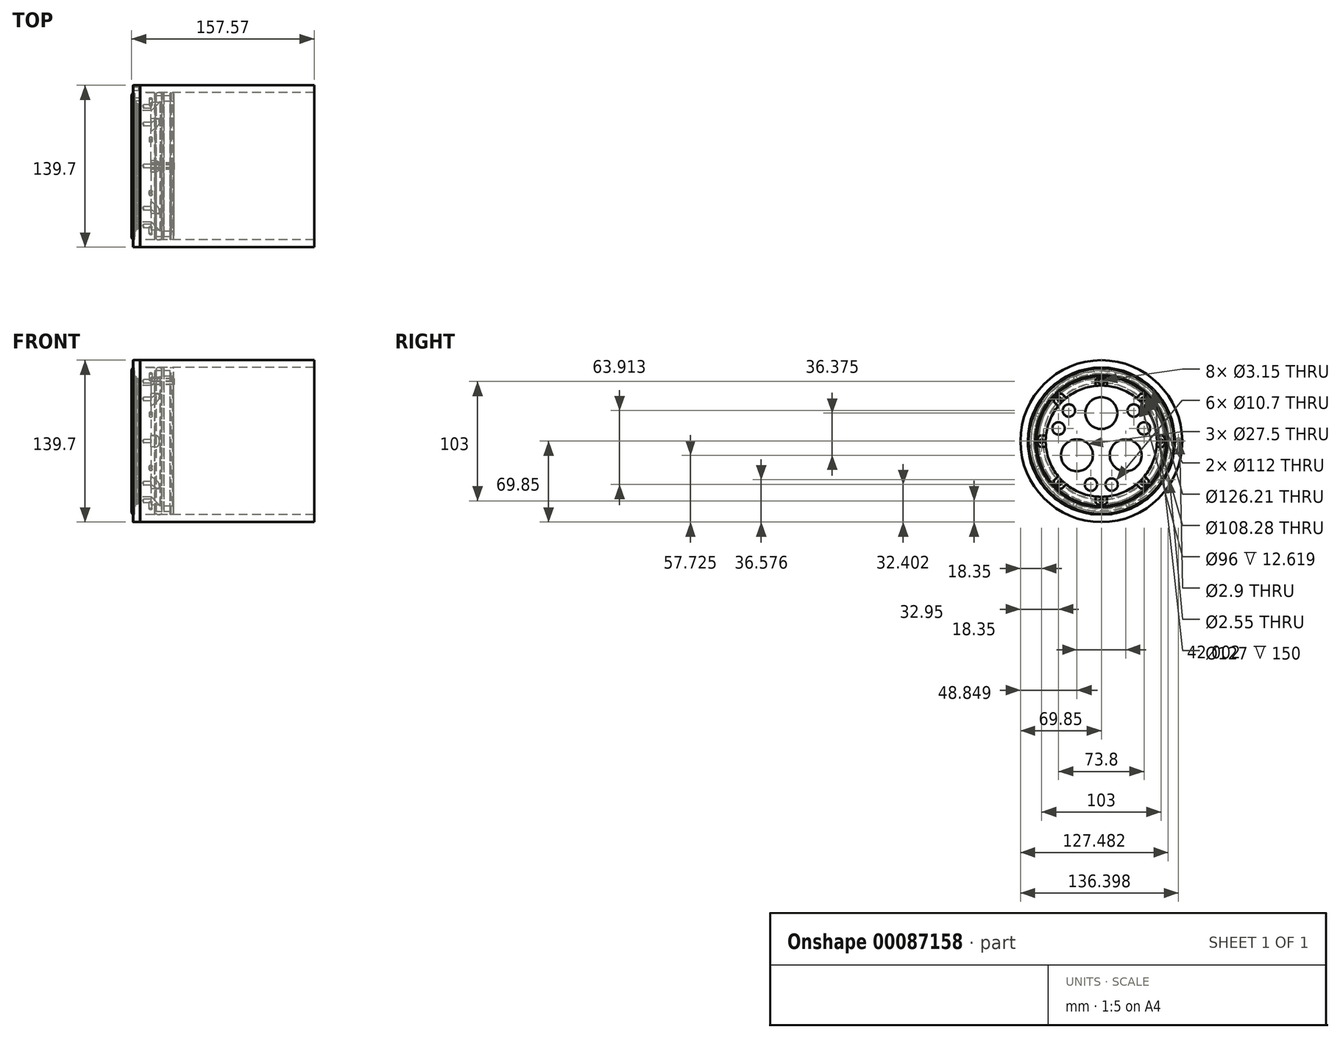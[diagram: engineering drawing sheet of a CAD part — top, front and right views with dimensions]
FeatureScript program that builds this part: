
annotation { "Feature Type Name" : "Feature", "Feature Type Description" : "" }
export const myFeature = defineFeature(function(context is Context, id is Id, definition is map)
    precondition{}
    {
        {
            assignVariable(context, id + "F0", {"name" : "M3_Helicoil_Drill_Depth", "anyValue" : 6.5});
        }
        {
            var Q0;
            Q0=qCreatedBy(makeId("Front.planeOp"),FACE);
            var sketch = newSketch(context, id + "F1", { "sketchPlane" : qUnion([Q0])});
            skLineSegment(sketch, "E0", {"start": v(0, 69.85) * mm, "end": v(6.25, 69.85) * mm});
            skLineSegment(sketch, "E1", {"start": v(6.25, 69.85) * mm, "end": v(6.25, 63.25) * mm});
            skLineSegment(sketch, "E2", {"start": v(6.25, 63.25) * mm, "end": v(35, 63.25) * mm, "construction": true});
            skLineSegment(sketch, "E3", {"start": v(35, 63.25) * mm, "end": v(35, 56) * mm});
            skLineSegment(sketch, "E4", {"start": v(35, 56) * mm, "end": v(23.5, 56) * mm});
            skLineSegment(sketch, "E5", {"start": v(23.5, 56) * mm, "end": v(15.5, 48) * mm});
            skLineSegment(sketch, "E6", {"start": v(15.5, 48) * mm, "end": v(2.38, 48) * mm});
            skLineSegment(sketch, "E7", {"start": v(2.38, 48) * mm, "end": v(2.38, 56) * mm, "construction": true});
            skLineSegment(sketch, "E8", {"start": v(2.38, 56) * mm, "end": v(0, 56) * mm});
            skLineSegment(sketch, "E9", {"start": v(0, 56) * mm, "end": v(0, 69.85) * mm, "construction": true});
            skLineSegment(sketch, "E10", {"start": v(6.25, 63.25) * mm, "end": v(19, 63.25) * mm});
            skLineSegment(sketch, "E11", {"start": v(19, 63.25) * mm, "end": v(19, 60.83) * mm});
            skLineSegment(sketch, "E12", {"start": v(19, 60.83) * mm, "end": v(24.54, 60.83) * mm});
            skLineSegment(sketch, "E13", {"start": v(24.54, 60.83) * mm, "end": v(24.54, 63.25) * mm});
            skLineSegment(sketch, "E14", {"start": v(24.54, 63.25) * mm, "end": v(25.54, 63.25) * mm});
            skLineSegment(sketch, "E15", {"start": v(25.54, 63.25) * mm, "end": v(25.54, 56) * mm, "construction": true});
            skLineSegment(sketch, "E16.MirrorCS", {"start": v(26.54, 63.25) * mm, "end": v(25.54, 63.25) * mm});
            skLineSegment(sketch, "E17.MirrorCS", {"start": v(26.54, 60.83) * mm, "end": v(26.54, 63.25) * mm});
            skLineSegment(sketch, "E18.MirrorCS", {"start": v(32.07, 60.83) * mm, "end": v(26.54, 60.83) * mm});
            skLineSegment(sketch, "E19.MirrorCS", {"start": v(32.07, 63.25) * mm, "end": v(32.07, 60.83) * mm});
            skLineSegment(sketch, "E20", {"start": v(32.07, 63.25) * mm, "end": v(35, 63.25) * mm});
            skLineSegment(sketch, "E21", {"start": v(0, 0) * mm, "end": v(57.37, 0) * mm, "construction": true});
            skLineSegment(sketch, "E22", {"start": v(0, 69.85) * mm, "end": v(0, 63.1) * mm});
            skLineSegment(sketch, "E23", {"start": v(0, 63.1) * mm, "end": v(1.32, 63.1) * mm});
            skLineSegment(sketch, "E24", {"start": v(1.32, 63.1) * mm, "end": v(1.32, 58.53) * mm});
            skLineSegment(sketch, "E25", {"start": v(1.32, 58.53) * mm, "end": v(0, 58.53) * mm});
            skLineSegment(sketch, "E26", {"start": v(0, 58.53) * mm, "end": v(0, 56) * mm});
            skLineSegment(sketch, "E27", {"start": v(2.38, 48) * mm, "end": v(2.38, 50.63) * mm});
            skLineSegment(sketch, "E28", {"start": v(2.38, 50.63) * mm, "end": v(4.31, 50.63) * mm});
            skLineSegment(sketch, "E29", {"start": v(4.31, 50.63) * mm, "end": v(4.31, 54.14) * mm});
            skLineSegment(sketch, "E30", {"start": v(4.31, 54.14) * mm, "end": v(2.38, 54.14) * mm});
            skLineSegment(sketch, "E31", {"start": v(2.38, 54.14) * mm, "end": v(2.38, 56) * mm});
            skLineSegment(sketch, "E32", {"start": v(-1, 89.78) * mm, "end": v(37.1, 89.78) * mm, "construction": true});
            skSolve(sketch);
        }
        {
            var Q0;
            Q0 = qSketchRegion(id + "F1", true);
            var Q1;
            Q1=sQuery(id+"F1.wireOp",EDGE,"E21");
            revolve(context, id + "F2", {"entities" : qUnion([Q0]), "axis" : qUnion([Q1]), "revolveType" : RevolveType.FULL});
        }
        {
            var Q0;
            Q0=makeQuery(id+"F2.opRevolve","SWEPT_FACE",FACE,{"disambiguationData":[OSD([sQuery(id+"F1.wireOp",EDGE,"E1")])]});
            var sketch = newSketch(context, id + "F3", { "sketchPlane" : qUnion([Q0])});
            skCircle(sketch, "E33", {"center": v(0, 0) * mm, "radius": 66.55 * mm, "construction": true});
            skLineSegment(sketch, "E34", {"start": v(0, 0) * mm, "end": v(66.55, 0) * mm, "construction": true});
            skLineSegment(sketch, "E35.1.0", {"start": v(0, 0) * mm, "end": v(57.63, 33.27) * mm, "construction": true});
            skLineSegment(sketch, "E35.2.0", {"start": v(0, 0) * mm, "end": v(33.27, 57.63) * mm, "construction": true});
            skLineSegment(sketch, "E36.1.3.0", {"start": v(0, 0) * mm, "end": v(0, 66.55) * mm, "construction": true});
            skLineSegment(sketch, "E36.1.4.0", {"start": v(0, 0) * mm, "end": v(-33.27, 57.63) * mm, "construction": true});
            skLineSegment(sketch, "E36.1.5.0", {"start": v(0, 0) * mm, "end": v(-57.63, 33.27) * mm, "construction": true});
            skLineSegment(sketch, "E37.1.6.0", {"start": v(0, 0) * mm, "end": v(-66.55, 0) * mm, "construction": true});
            skLineSegment(sketch, "E37.1.7.0", {"start": v(0, 0) * mm, "end": v(-57.63, -33.27) * mm, "construction": true});
            skLineSegment(sketch, "E38.1.8.0", {"start": v(0, 0) * mm, "end": v(-33.27, -57.63) * mm, "construction": true});
            skLineSegment(sketch, "E38.1.9.0", {"start": v(0, 0) * mm, "end": v(0, -66.55) * mm, "construction": true});
            skLineSegment(sketch, "E38.1.10.0", {"start": v(0, 0) * mm, "end": v(33.27, -57.63) * mm, "construction": true});
            skLineSegment(sketch, "E38.1.11.0", {"start": v(0, 0) * mm, "end": v(57.63, -33.27) * mm, "construction": true});
            skLineSegment(sketch, "E39", {"start": v(69.85, 0) * mm, "end": v(63.25, 0) * mm, "construction": true});
            skSolve(sketch);
        }
        {
            var Q0;
            Q0=qCreatedBy(makeId("Top.planeOp"),FACE);
            var Q1;
            Q1=sQuery(id+"F1.wireOp",VERTEX,"E10.end");
            cPlane(context, id + "F4", {"entities" : qUnion([Q0, Q1]), "cplaneType" : CPlaneType.PLANE_POINT, "offset" : 150 * mm, "width" : 150 * mm, "height" : 150 * mm});
        }
        {
            var Q0;
            Q0=qCreatedBy(id+"F4.planeOp",FACE);
            var sketch = newSketch(context, id + "F5", { "sketchPlane" : qUnion([Q0])});
            skPoint(sketch, "E40", {"position": v(15.25, 0) * mm});
            skLineSegment(sketch, "E41.0", {"start": v(6.25, -69.85) * mm, "end": v(6.25, 69.85) * mm, "construction": true});
            skLineSegment(sketch, "E41.1", {"start": v(19, -63.25) * mm, "end": v(19, 63.25) * mm, "construction": true});
            skLineSegment(sketch, "E42", {"start": v(6.25, 0) * mm, "end": v(19, 0) * mm, "construction": true});
            skCircle(sketch, "E43", {"center": v(15.25, 0) * mm, "radius": 1.5 * mm, "construction": true});
            skCircle(sketch, "E44", {"center": v(15.25, 0) * mm, "radius": 2.75 * mm, "construction": true});
            skSolve(sketch);
        }
        {
            var Q0;
            Q0=makeQuery(id+"F2.opRevolve","SWEPT_EDGE",EDGE,{"disambiguationData":[OSD([sQuery(id+"F1.wireOp",EDGE,"E3"),sQuery(id+"F1.wireOp",EDGE,"E20")])]});
            chamfer(context, id + "F6", {"entities" : qUnion([Q0]), "chamferType" : ChamferType.OFFSET_ANGLE, "width" : 2 * mm, "oppositeDirection" : false, "angle" : 10 * degree, "tangentPropagation" : true});
        }
        {
            var Q0;
            Q0=makeQuery(id+"F2.opRevolve","SWEPT_EDGE",EDGE,{"disambiguationData":[OSD([sQuery(id+"F1.wireOp",EDGE,"E8"),sQuery(id+"F1.wireOp",EDGE,"E26")])]});
            var Q1;
            Q1=makeQuery(id+"F2.opRevolve","SWEPT_EDGE",EDGE,{"disambiguationData":[OSD([sQuery(id+"F1.wireOp",EDGE,"E6"),sQuery(id+"F1.wireOp",EDGE,"E27")])]});
            chamfer(context, id + "F7", {"entities" : qUnion([Q0, Q1]), "width" : .5 * mm, "tangentPropagation" : true});
        }
        {
            var Q0;
            Q0=makeQuery(id+"F2.opRevolve","SWEPT_EDGE",EDGE,{"disambiguationData":[OSD([sQuery(id+"F1.wireOp",EDGE,"E3"),sQuery(id+"F1.wireOp",EDGE,"E4")])]});
            chamfer(context, id + "F8", {"entities" : qUnion([Q0]), "width" : 1 * mm, "tangentPropagation" : true});
        }
        {
            var Q0;
            Q0=makeQuery(id+"F2.opRevolve","SWEPT_FACE",FACE,{"disambiguationData":[OSD([sQuery(id+"F1.wireOp",EDGE,"E24")])]});
            fillet(context, id + "F9", {"entities" : qUnion([Q0]), "radius" : 0.2 * mm, "tangentPropagation" : true, "allowEdgeOverflow" : false});
        }
        {
            var Q0;
            Q0=makeQuery(id+"F2.opRevolve","SWEPT_FACE",FACE,{"disambiguationData":[OSD([sQuery(id+"F1.wireOp",EDGE,"E29")])]});
            fillet(context, id + "F10", {"entities" : qUnion([Q0]), "radius" : 0.2 * mm, "allowEdgeOverflow" : false});
        }
        {
            var Q0;
            Q0=makeQuery(id+"F2.opRevolve","SWEPT_FACE",FACE,{"disambiguationData":[OSD([sQuery(id+"F1.wireOp",EDGE,"E18.MirrorCS")])]});
            var Q1;
            Q1=makeQuery(id+"F2.opRevolve","SWEPT_FACE",FACE,{"disambiguationData":[OSD([sQuery(id+"F1.wireOp",EDGE,"E12")])]});
            fillet(context, id + "F11", {"entities" : qUnion([Q0, Q1]), "radius" : 0.2 * mm, "tangentPropagation" : true, "allowEdgeOverflow" : false});
        }
        {
            var Q0;
            Q0=makeQuery(id+"F2.opRevolve","SWEPT_EDGE",EDGE,{"disambiguationData":[OSD([sQuery(id+"F1.wireOp",EDGE,"E10"),sQuery(id+"F1.wireOp",EDGE,"E11")])]});
            var Q1;
            Q1=makeQuery(id+"F2.opRevolve","SWEPT_EDGE",EDGE,{"disambiguationData":[OSD([sQuery(id+"F1.wireOp",EDGE,"E13"),sQuery(id+"F1.wireOp",EDGE,"E14")])]});
            var Q2;
            Q2=makeQuery(id+"F2.opRevolve","SWEPT_EDGE",EDGE,{"disambiguationData":[OSD([sQuery(id+"F1.wireOp",EDGE,"E16.MirrorCS"),sQuery(id+"F1.wireOp",EDGE,"E17.MirrorCS")])]});
            var Q3;
            Q3=makeQuery(id+"F2.opRevolve","SWEPT_EDGE",EDGE,{"disambiguationData":[OSD([sQuery(id+"F1.wireOp",EDGE,"E19.MirrorCS"),sQuery(id+"F1.wireOp",EDGE,"E20")])]});
            var Q4;
            Q4=makeQuery(id+"F2.opRevolve","SWEPT_EDGE",EDGE,{"disambiguationData":[OSD([sQuery(id+"F1.wireOp",EDGE,"E0"),sQuery(id+"F1.wireOp",EDGE,"E1")])]});
            var Q5;
            Q5=makeQuery(id+"F2.opRevolve","SWEPT_EDGE",EDGE,{"disambiguationData":[OSD([sQuery(id+"F1.wireOp",EDGE,"E0"),sQuery(id+"F1.wireOp",EDGE,"E22")])]});
            var Q6;
            Q6=makeQuery(id+"F2.opRevolve","SWEPT_EDGE",EDGE,{"disambiguationData":[OSD([sQuery(id+"F1.wireOp",EDGE,"E1"),sQuery(id+"F1.wireOp",EDGE,"E10")])]});
            var Q7;
            Q7=makeQuery(id+"F2.opRevolve","SWEPT_EDGE",EDGE,{"disambiguationData":[OSD([sQuery(id+"F1.wireOp",EDGE,"E22"),sQuery(id+"F1.wireOp",EDGE,"E23")])]});
            var Q8;
            Q8=makeQuery(id+"F2.opRevolve","SWEPT_EDGE",EDGE,{"disambiguationData":[OSD([sQuery(id+"F1.wireOp",EDGE,"E25"),sQuery(id+"F1.wireOp",EDGE,"E26")])]});
            var Q9;
            Q9=makeQuery(id+"F2.opRevolve","SWEPT_EDGE",EDGE,{"disambiguationData":[OSD([sQuery(id+"F1.wireOp",EDGE,"E30"),sQuery(id+"F1.wireOp",EDGE,"E31")])]});
            var Q10;
            Q10=makeQuery(id+"F2.opRevolve","SWEPT_EDGE",EDGE,{"disambiguationData":[OSD([sQuery(id+"F1.wireOp",EDGE,"E27"),sQuery(id+"F1.wireOp",EDGE,"E28")])]});
            var Q11;
            {var subQ0=sQuery(id+"F1.wireOp",EDGE,"E3");Q11=makeQuery(id+"F6.opChamfer","BLEND_EDGE",EDGE,{"blendedFrom":[makeQuery(id+"F2.opRevolve","SWEPT_EDGE",EDGE,{"disambiguationData":[OSD([subQ0,sQuery(id+"F1.wireOp",EDGE,"E20")])]}),makeQuery(id+"F2.opRevolve","SWEPT_FACE",FACE,{"disambiguationData":[OSD([subQ0])]})],"blendedInto":[makeQuery(id+"F2.opRevolve","SWEPT_FACE",FACE,{"disambiguationData":[OSD([subQ0])]})]});}
            var Q12;
            Q12=makeQuery(id+"F2.opRevolve","SWEPT_EDGE",EDGE,{"disambiguationData":[OSD([sQuery(id+"F1.wireOp",EDGE,"E8"),sQuery(id+"F1.wireOp",EDGE,"E31")])]});
            chamfer(context, id + "F12", {"entities" : qUnion([Q0, Q1, Q2, Q3, Q4, Q5, Q6, Q7, Q8, Q9, Q10, Q11, Q12]), "width" : 0.25 * mm, "tangentPropagation" : true});
        }
        {
            var Q0;
            Q0=sQuery(id+"F3.wireOp",VERTEX,"E34.end");
            var Q1;
            Q1=makeQuery(id+"F2.opRevolve","SWEPT_BODY",BODY,{"disambiguationData":[OSD([sQuery(id+"F1.wireOp",EDGE,"E0"),sQuery(id+"F1.wireOp",EDGE,"E1"),sQuery(id+"F1.wireOp",EDGE,"E3"),sQuery(id+"F1.wireOp",EDGE,"EppfiJ0T-nPKM-5v7P-hZBO-1SXBlnIL5BD0"),sQuery(id+"F1.wireOp",EDGE,"E4"),sQuery(id+"F1.wireOp",EDGE,"E5"),sQuery(id+"F1.wireOp",EDGE,"E6"),sQuery(id+"F1.wireOp",EDGE,"E7"),sQuery(id+"F1.wireOp",EDGE,"E8"),sQuery(id+"F1.wireOp",EDGE,"E9"),sQuery(id+"F1.wireOp",EDGE,"E10"),sQuery(id+"F1.wireOp",EDGE,"E11"),sQuery(id+"F1.wireOp",EDGE,"E12"),sQuery(id+"F1.wireOp",EDGE,"E13"),sQuery(id+"F1.wireOp",EDGE,"E14"),sQuery(id+"F1.wireOp",EDGE,"E16.MirrorCS"),sQuery(id+"F1.wireOp",EDGE,"E17.MirrorCS"),sQuery(id+"F1.wireOp",EDGE,"E18.MirrorCS"),sQuery(id+"F1.wireOp",EDGE,"E19.MirrorCS"),sQuery(id+"F1.wireOp",EDGE,"E20")])]});
            hole(context, id + "F13", {"style" : HoleStyle.C_SINK, "endStyle" : HoleEndStyle.THROUGH, "standardTappedOrClearance" : lookupTablePath({ "fit" : "Normal", "standard" : "ISO", "size" : "M2.5", "type" : "Clearance" }), "standardBlindInLast" : lookupTablePath({ "fit" : "Normal", "standard" : "ISO", "engagement" : "75%", "pitch" : "0.35 mm", "size" : "M2.5", "type" : "Clearance & tapped" }), "holeDiameter" : 2.9 * mm, "cSinkDiameter" : 5.5 * mm, "cSinkAngle" : 90 * degree, "majorDiameter" : 5 * mm, "locations" : qUnion([Q0]), "scope" : qUnion([Q1]), "tappedDepth" : 12 * mm, "tapClearance" : 3});
        }
        {
            var Q0;
            Q0=sQuery(id+"F3.wireOp",VERTEX,"E38.1.11.0.end");
            var Q1;
            Q1=makeQuery(id+"F2.opRevolve","SWEPT_BODY",BODY,{"disambiguationData":[OSD([sQuery(id+"F1.wireOp",EDGE,"E0"),sQuery(id+"F1.wireOp",EDGE,"E1"),sQuery(id+"F1.wireOp",EDGE,"E3"),sQuery(id+"F1.wireOp",EDGE,"EppfiJ0T-nPKM-5v7P-hZBO-1SXBlnIL5BD0"),sQuery(id+"F1.wireOp",EDGE,"E4"),sQuery(id+"F1.wireOp",EDGE,"E5"),sQuery(id+"F1.wireOp",EDGE,"E6"),sQuery(id+"F1.wireOp",EDGE,"E7"),sQuery(id+"F1.wireOp",EDGE,"E8"),sQuery(id+"F1.wireOp",EDGE,"E9"),sQuery(id+"F1.wireOp",EDGE,"E10"),sQuery(id+"F1.wireOp",EDGE,"E11"),sQuery(id+"F1.wireOp",EDGE,"E12"),sQuery(id+"F1.wireOp",EDGE,"E13"),sQuery(id+"F1.wireOp",EDGE,"E14"),sQuery(id+"F1.wireOp",EDGE,"E16.MirrorCS"),sQuery(id+"F1.wireOp",EDGE,"E17.MirrorCS"),sQuery(id+"F1.wireOp",EDGE,"E18.MirrorCS"),sQuery(id+"F1.wireOp",EDGE,"E19.MirrorCS"),sQuery(id+"F1.wireOp",EDGE,"E20")])]});
            hole(context, id + "F14", {"style" : HoleStyle.SIMPLE, "endStyle" : HoleEndStyle.THROUGH, "holeDiameter" : 2.55 * mm, "majorDiameter" : 3 * mm, "locations" : qUnion([Q0]), "scope" : qUnion([Q1]), "isTappedThrough" : true, "tappedDepth" : 12 * mm, "tapClearance" : 3});
        }
        {
            var Q0;
            Q0=makeQuery(id+"F2.opRevolve","SWEPT_FACE",FACE,{"disambiguationData":[OSD([sQuery(id+"F1.wireOp",EDGE,"E31")])]});
            var sketch = newSketch(context, id + "F15", { "sketchPlane" : qUnion([Q0])});
            skCircle(sketch, "E45", {"center": v(0, 0) * mm, "radius": 55.9 * mm});
            skCircle(sketch, "E46.0", {"center": v(0, 0) * mm, "radius": 56 * mm, "construction": true});
            skCircle(sketch, "E47", {"center": v(0, 24.25) * mm, "radius": 19.05 * mm, "construction": true});
            skCircle(sketch, "E48", {"center": v(-21, -12.12) * mm, "radius": 19.05 * mm, "construction": true});
            skCircle(sketch, "E49", {"center": v(0, 0) * mm, "radius": 24.25 * mm, "construction": true});
            skCircle(sketch, "E50", {"center": v(21, -12.12) * mm, "radius": 19.05 * mm, "construction": true});
            skLineSegment(sketch, "E51", {"start": v(-21, -12.13) * mm, "end": v(0, 0) * mm, "construction": true});
            skLineSegment(sketch, "E52", {"start": v(21, -12.12) * mm, "end": v(0, 0) * mm, "construction": true});
            skLineSegment(sketch, "E53", {"start": v(0, 24.25) * mm, "end": v(0, 0) * mm, "construction": true});
            skCircle(sketch, "E54", {"center": v(0, 24.25) * mm, "radius": 13.75 * mm});
            skCircle(sketch, "E55", {"center": v(-21, -12.12) * mm, "radius": 13.75 * mm});
            skCircle(sketch, "E56", {"center": v(21, -12.12) * mm, "radius": 13.75 * mm});
            skCircle(sketch, "E57", {"center": v(-36.9, 10.98) * mm, "radius": 8.25 * mm, "construction": true});
            skCircle(sketch, "E58", {"center": v(0, 0) * mm, "radius": 38.5 * mm, "construction": true});
            skCircle(sketch, "E59", {"center": v(-27.96, 26.46) * mm, "radius": 8.25 * mm, "construction": true});
            skLineSegment(sketch, "E60", {"start": v(0, 0) * mm, "end": v(-33.34, 19.25) * mm, "construction": true});
            skLineSegment(sketch, "E61", {"start": v(0, 0) * mm, "end": v(33.34, 19.25) * mm, "construction": true});
            skLineSegment(sketch, "E62", {"start": v(0, 0) * mm, "end": v(0, -38.5) * mm, "construction": true});
            skCircle(sketch, "E63", {"center": v(-27.96, 26.46) * mm, "radius": 5.35 * mm});
            skCircle(sketch, "E64", {"center": v(-36.9, 10.98) * mm, "radius": 5.35 * mm});
            skCircle(sketch, "E65.1.0", {"center": v(8.94, -37.45) * mm, "radius": 5.35 * mm});
            skCircle(sketch, "E65.1.1", {"center": v(8.94, -37.45) * mm, "radius": 8.25 * mm, "construction": true});
            skCircle(sketch, "E65.1.2", {"center": v(-8.94, -37.45) * mm, "radius": 5.35 * mm});
            skCircle(sketch, "E65.1.3", {"center": v(-8.94, -37.45) * mm, "radius": 8.25 * mm, "construction": true});
            skCircle(sketch, "E65.2.0", {"center": v(27.96, 26.46) * mm, "radius": 5.35 * mm});
            skCircle(sketch, "E65.2.1", {"center": v(27.96, 26.46) * mm, "radius": 8.25 * mm, "construction": true});
            skCircle(sketch, "E65.2.2", {"center": v(36.9, 10.98) * mm, "radius": 5.35 * mm});
            skCircle(sketch, "E65.2.3", {"center": v(36.9, 10.98) * mm, "radius": 8.25 * mm, "construction": true});
            skSolve(sketch);
        }
        {
            var Q0;
            Q0 = qSketchRegion(id + "F15", true);
            extrude(context, id + "F16", {"entities" : qUnion([Q0]), "offsetDistance" : 25 * mm, "depth" : 1 / 203.2 * mm});
        }
        {
            var Q0;
            Q0=qCreatedBy(makeId("Top.planeOp"),FACE);
            cPlane(context, id + "F17", {"entities" : qUnion([Q0]), "cplaneType" : CPlaneType.OFFSET, "offset" : 5.5 / 50.8 * mm, "width" : 150 * mm, "height" : 150 * mm});
        }
        {
            var Q0;
            Q0=qCreatedBy(makeId("Front.planeOp"),FACE);
            var sketch = newSketch(context, id + "F18", { "sketchPlane" : qUnion([Q0])});
            skLineSegment(sketch, "E66", {"start": v(15.5, -48) * mm, "end": v(2.88, -48) * mm});
            skLineSegment(sketch, "E67", {"start": v(2.88, 48) * mm, "end": v(15.5, 48) * mm});
            skLineSegment(sketch, "E68", {"start": v(15.5, 48) * mm, "end": v(23.5, 56) * mm});
            skLineSegment(sketch, "E69", {"start": v(23.5, -56) * mm, "end": v(15.5, -48) * mm});
            skLineSegment(sketch, "E70", {"start": v(34, -56) * mm, "end": v(23.5, -56) * mm});
            skLineSegment(sketch, "E71", {"start": v(23.5, 56) * mm, "end": v(34, 56) * mm});
            skLineSegment(sketch, "E72", {"start": v(34, 56) * mm, "end": v(35, 57) * mm});
            skLineSegment(sketch, "E73", {"start": v(35, -57) * mm, "end": v(34, -56) * mm});
            skLineSegment(sketch, "E74", {"start": v(35, 57) * mm, "end": v(35, 62.68) * mm});
            skLineSegment(sketch, "E75", {"start": v(35, -62.68) * mm, "end": v(35, -57) * mm});
            skLineSegment(sketch, "E76", {"start": v(34.8, -62.93) * mm, "end": v(35, -62.68) * mm});
            skLineSegment(sketch, "E77", {"start": v(35, 62.68) * mm, "end": v(34.8, 62.93) * mm});
            skLineSegment(sketch, "E78", {"start": v(33, -63.25) * mm, "end": v(34.8, -62.93) * mm});
            skLineSegment(sketch, "E79", {"start": v(34.8, 62.93) * mm, "end": v(33, 63.25) * mm});
            skLineSegment(sketch, "E80", {"start": v(32.32, -63.25) * mm, "end": v(33, -63.25) * mm});
            skLineSegment(sketch, "E81", {"start": v(33, 63.25) * mm, "end": v(32.32, 63.25) * mm});
            skLineSegment(sketch, "E82", {"start": v(32.32, 63.25) * mm, "end": v(32.07, 63) * mm});
            skLineSegment(sketch, "E83", {"start": v(32.07, -63) * mm, "end": v(32.32, -63.25) * mm});
            skLineSegment(sketch, "E84", {"start": v(32.07, 61.03) * mm, "end": v(32.07, 63) * mm});
            skLineSegment(sketch, "E85", {"start": v(32.07, -63) * mm, "end": v(32.07, -61.03) * mm});
            skArc(sketch, "E86", {"start": v(31.87, 60.83) * mm, "mid": v(32.02, 60.9) * mm, "end": v(32.07, 61.03) * mm});
            skArc(sketch, "E87", {"start": v(32.07, -61.03) * mm, "mid": v(32.02, -60.9) * mm, "end": v(31.87, -60.83) * mm});
            skLineSegment(sketch, "E88", {"start": v(31.87, -60.83) * mm, "end": v(26.74, -60.83) * mm});
            skLineSegment(sketch, "E89", {"start": v(26.74, 60.83) * mm, "end": v(31.87, 60.83) * mm});
            skArc(sketch, "E90", {"start": v(26.74, -60.83) * mm, "mid": v(26.6, -60.9) * mm, "end": v(26.54, -61.03) * mm});
            skArc(sketch, "E91", {"start": v(26.54, 61.03) * mm, "mid": v(26.6, 60.9) * mm, "end": v(26.74, 60.83) * mm});
            skLineSegment(sketch, "E92", {"start": v(26.54, -61.03) * mm, "end": v(26.54, -63) * mm});
            skLineSegment(sketch, "E93", {"start": v(26.54, 63) * mm, "end": v(26.54, 61.03) * mm});
            skLineSegment(sketch, "E94", {"start": v(26.29, -63.25) * mm, "end": v(26.54, -63) * mm});
            skLineSegment(sketch, "E95", {"start": v(26.54, 63) * mm, "end": v(26.29, 63.25) * mm});
            skLineSegment(sketch, "E96", {"start": v(26.29, -63.25) * mm, "end": v(24.79, -63.25) * mm});
            skLineSegment(sketch, "E97", {"start": v(24.79, 63.25) * mm, "end": v(26.29, 63.25) * mm});
            skLineSegment(sketch, "E98", {"start": v(24.79, 63.25) * mm, "end": v(24.54, 63) * mm});
            skLineSegment(sketch, "E99", {"start": v(24.54, -63) * mm, "end": v(24.79, -63.25) * mm});
            skLineSegment(sketch, "E100", {"start": v(24.54, -61.03) * mm, "end": v(24.54, -63) * mm});
            skLineSegment(sketch, "E101", {"start": v(24.54, 63) * mm, "end": v(24.54, 61.03) * mm});
            skArc(sketch, "E102", {"start": v(24.54, -61.03) * mm, "mid": v(24.48, -60.9) * mm, "end": v(24.34, -60.83) * mm});
            skArc(sketch, "E103", {"start": v(24.34, 60.83) * mm, "mid": v(24.48, 60.9) * mm, "end": v(24.54, 61.03) * mm});
            skLineSegment(sketch, "E104", {"start": v(19.2, -60.83) * mm, "end": v(24.34, -60.83) * mm});
            skLineSegment(sketch, "E105", {"start": v(24.34, 60.83) * mm, "end": v(19.2, 60.83) * mm});
            skArc(sketch, "E106", {"start": v(19, 61.03) * mm, "mid": v(19.06, 60.9) * mm, "end": v(19.2, 60.83) * mm});
            skArc(sketch, "E107", {"start": v(19.2, -60.83) * mm, "mid": v(19.06, -60.9) * mm, "end": v(19, -61.03) * mm});
            skLineSegment(sketch, "E108", {"start": v(19, 61.03) * mm, "end": v(19, 63) * mm});
            skLineSegment(sketch, "E109", {"start": v(19, -63) * mm, "end": v(19, -61.03) * mm});
            skLineSegment(sketch, "E110", {"start": v(18.75, -63.25) * mm, "end": v(19, -63) * mm});
            skLineSegment(sketch, "E111", {"start": v(19, 63) * mm, "end": v(18.75, 63.25) * mm});
            skLineSegment(sketch, "E112", {"start": v(14.05, 63.25) * mm, "end": v(6.5, 63.25) * mm});
            skLineSegment(sketch, "E113", {"start": v(6.5, -63.25) * mm, "end": v(18.75, -63.25) * mm});
            skLineSegment(sketch, "E114", {"start": v(18.75, 63.25) * mm, "end": v(16.45, 63.25) * mm});
            skLineSegment(sketch, "E115", {"start": v(6.5, -63.25) * mm, "end": v(6.25, -63.5) * mm});
            skLineSegment(sketch, "E116", {"start": v(6.25, 63.5) * mm, "end": v(6.5, 63.25) * mm});
            skLineSegment(sketch, "E117", {"start": v(6.25, -65.27) * mm, "end": v(6.25, -63.5) * mm});
            skLineSegment(sketch, "E118", {"start": v(6.25, 63.5) * mm, "end": v(6.25, 65.27) * mm});
            skLineSegment(sketch, "E119", {"start": v(6.25, 67.82) * mm, "end": v(6.25, 69.6) * mm});
            skLineSegment(sketch, "E120", {"start": v(6.25, -69.6) * mm, "end": v(6.25, -67.82) * mm});
            skLineSegment(sketch, "E121", {"start": v(6, -69.85) * mm, "end": v(6.25, -69.6) * mm});
            skLineSegment(sketch, "E122", {"start": v(6.25, 69.6) * mm, "end": v(6, 69.85) * mm});
            skLineSegment(sketch, "E123", {"start": v(0.25, -69.85) * mm, "end": v(6, -69.85) * mm});
            skLineSegment(sketch, "E124", {"start": v(6, 69.85) * mm, "end": v(0.25, 69.85) * mm});
            skLineSegment(sketch, "E125", {"start": v(0.25, 69.85) * mm, "end": v(0, 69.6) * mm});
            skLineSegment(sketch, "E126", {"start": v(0, -69.6) * mm, "end": v(0.25, -69.85) * mm});
            skLineSegment(sketch, "E127", {"start": v(0, -65.27) * mm, "end": v(0, -63.36) * mm});
            skLineSegment(sketch, "E128", {"start": v(0, 63.36) * mm, "end": v(0, 65.27) * mm});
            skLineSegment(sketch, "E129", {"start": v(0, 67.82) * mm, "end": v(0, 69.6) * mm});
            skLineSegment(sketch, "E130", {"start": v(0, -69.6) * mm, "end": v(0, -67.82) * mm});
            skLineSegment(sketch, "E131", {"start": v(0.25, -63.1) * mm, "end": v(0, -63.36) * mm});
            skLineSegment(sketch, "E132", {"start": v(0, 63.36) * mm, "end": v(0.25, 63.1) * mm});
            skLineSegment(sketch, "E133", {"start": v(0.25, -63.1) * mm, "end": v(1.12, -63.1) * mm});
            skLineSegment(sketch, "E134", {"start": v(1.12, 63.1) * mm, "end": v(0.25, 63.1) * mm});
            skArc(sketch, "E135", {"start": v(1.32, 62.9) * mm, "mid": v(1.26, 63.05) * mm, "end": v(1.12, 63.1) * mm});
            skArc(sketch, "E136", {"start": v(1.12, -63.1) * mm, "mid": v(1.26, -63.05) * mm, "end": v(1.32, -62.9) * mm});
            skLineSegment(sketch, "E137", {"start": v(1.32, 58.73) * mm, "end": v(1.32, 62.9) * mm});
            skLineSegment(sketch, "E138", {"start": v(1.32, -62.9) * mm, "end": v(1.32, -58.73) * mm});
            skArc(sketch, "E139", {"start": v(1.12, 58.53) * mm, "mid": v(1.26, 58.6) * mm, "end": v(1.32, 58.73) * mm});
            skArc(sketch, "E140", {"start": v(1.32, -58.73) * mm, "mid": v(1.26, -58.6) * mm, "end": v(1.12, -58.53) * mm});
            skLineSegment(sketch, "E141", {"start": v(1.12, -58.53) * mm, "end": v(0.25, -58.53) * mm});
            skLineSegment(sketch, "E142", {"start": v(0.25, 58.53) * mm, "end": v(1.12, 58.53) * mm});
            skLineSegment(sketch, "E143", {"start": v(0.25, 58.53) * mm, "end": v(0, 58.28) * mm});
            skLineSegment(sketch, "E144", {"start": v(0, -58.28) * mm, "end": v(0.25, -58.53) * mm});
            skLineSegment(sketch, "E145", {"start": v(0, 56.5) * mm, "end": v(0, 58.28) * mm});
            skLineSegment(sketch, "E146", {"start": v(0, -58.28) * mm, "end": v(0, -56.5) * mm});
            skLineSegment(sketch, "E147", {"start": v(0.5, -56) * mm, "end": v(0, -56.5) * mm});
            skLineSegment(sketch, "E148", {"start": v(0, 56.5) * mm, "end": v(0.5, 56) * mm});
            skLineSegment(sketch, "E149", {"start": v(2.38, -56) * mm, "end": v(0.5, -56) * mm});
            skLineSegment(sketch, "E150", {"start": v(2.38, -54.4) * mm, "end": v(2.38, -56) * mm});
            skLineSegment(sketch, "E151", {"start": v(2.63, -54.14) * mm, "end": v(2.38, -54.4) * mm});
            skLineSegment(sketch, "E152", {"start": v(2.38, 54.4) * mm, "end": v(2.63, 54.14) * mm});
            skLineSegment(sketch, "E153", {"start": v(4.11, -54.14) * mm, "end": v(2.63, -54.14) * mm});
            skLineSegment(sketch, "E154", {"start": v(2.63, 54.14) * mm, "end": v(4.11, 54.14) * mm});
            skArc(sketch, "E155", {"start": v(4.11, -54.14) * mm, "mid": v(4.25, -54.08) * mm, "end": v(4.31, -53.94) * mm});
            skArc(sketch, "E156", {"start": v(4.31, 53.94) * mm, "mid": v(4.25, 54.08) * mm, "end": v(4.11, 54.14) * mm});
            skLineSegment(sketch, "E157", {"start": v(4.31, -50.83) * mm, "end": v(4.31, -53.94) * mm});
            skLineSegment(sketch, "E158", {"start": v(4.31, 53.94) * mm, "end": v(4.31, 50.83) * mm});
            skArc(sketch, "E159", {"start": v(4.31, -50.83) * mm, "mid": v(4.25, -50.7) * mm, "end": v(4.11, -50.63) * mm});
            skArc(sketch, "E160", {"start": v(4.11, 50.63) * mm, "mid": v(4.25, 50.7) * mm, "end": v(4.31, 50.83) * mm});
            skLineSegment(sketch, "E161", {"start": v(2.63, -50.63) * mm, "end": v(4.11, -50.63) * mm});
            skLineSegment(sketch, "E162", {"start": v(4.11, 50.63) * mm, "end": v(2.63, 50.63) * mm});
            skLineSegment(sketch, "E163", {"start": v(2.63, 50.63) * mm, "end": v(2.38, 50.38) * mm});
            skLineSegment(sketch, "E164", {"start": v(2.38, -50.38) * mm, "end": v(2.63, -50.63) * mm});
            skLineSegment(sketch, "E165", {"start": v(2.38, -48.5) * mm, "end": v(2.38, -50.38) * mm});
            skLineSegment(sketch, "E166", {"start": v(2.38, 50.38) * mm, "end": v(2.38, 48.5) * mm});
            skLineSegment(sketch, "E167", {"start": v(2.88, -48) * mm, "end": v(2.38, -48.5) * mm});
            skLineSegment(sketch, "E168", {"start": v(2.38, 48.5) * mm, "end": v(2.88, 48) * mm});
            skLineSegment(sketch, "E169", {"start": v(2.13, -56) * mm, "end": v(0.5, -56) * mm});
            skLineSegment(sketch, "E170", {"start": v(0.5, 56) * mm, "end": v(2.13, 56) * mm});
            skLineSegment(sketch, "E171", {"start": v(2.13, -56) * mm, "end": v(2.38, -55.75) * mm});
            skLineSegment(sketch, "E172", {"start": v(2.38, 55.75) * mm, "end": v(2.13, 56) * mm});
            skLineSegment(sketch, "E173", {"start": v(2.38, -54.4) * mm, "end": v(2.38, -55.75) * mm});
            skLineSegment(sketch, "E174", {"start": v(2.38, 55.75) * mm, "end": v(2.38, 54.4) * mm});
            skLineSegment(sketch, "E175", {"start": v(0, 65.27) * mm, "end": v(0, 67.82) * mm});
            skLineSegment(sketch, "E176", {"start": v(6.25, 65.27) * mm, "end": v(6.25, 67.82) * mm});
            skLineSegment(sketch, "E177", {"start": v(14.05, 63.25) * mm, "end": v(16.45, 63.25) * mm});
            skLineSegment(sketch, "E178", {"start": v(0, 0) * mm, "end": v(54.33, 0) * mm});
            skSolve(sketch);
        }
        {
            var Q0;
            Q0=qCreatedBy(makeId("Front.planeOp"),FACE);
            var sketch = newSketch(context, id + "F19", { "sketchPlane" : qUnion([Q0])});
            skLineSegment(sketch, "E179", {"start": v(310.8, -69.85) * mm, "end": v(6, -69.85) * mm, "construction": true});
            skLineSegment(sketch, "E180", {"start": v(6, 69.85) * mm, "end": v(310.8, 69.85) * mm, "construction": true});
            skLineSegment(sketch, "E181", {"start": v(0, -69.85) * mm, "end": v(5.5, -69.85) * mm, "construction": true});
            skLineSegment(sketch, "E182", {"start": v(5.5, 69.85) * mm, "end": v(0, 69.85) * mm, "construction": true});
            skLineSegment(sketch, "E183", {"start": v(310.8, -63.5) * mm, "end": v(6, -63.5) * mm, "construction": true});
            skLineSegment(sketch, "E184", {"start": v(6, 63.5) * mm, "end": v(310.8, 63.5) * mm, "construction": true});
            skLineSegment(sketch, "E185", {"start": v(19.2, -60.83) * mm, "end": v(24.34, -60.83) * mm, "construction": true});
            skLineSegment(sketch, "E186", {"start": v(24.34, 60.83) * mm, "end": v(19.2, 60.83) * mm, "construction": true});
            skLineSegment(sketch, "E187", {"start": v(19, 61.03) * mm, "end": v(19, 63) * mm, "construction": true});
            skLineSegment(sketch, "E188", {"start": v(19, -63) * mm, "end": v(19, -61.03) * mm, "construction": true});
            skLineSegment(sketch, "E189", {"start": v(24.54, -61.03) * mm, "end": v(24.54, -63) * mm, "construction": true});
            skLineSegment(sketch, "E190", {"start": v(24.54, 63) * mm, "end": v(24.54, 61.03) * mm, "construction": true});
            skEllipse(sketch, "E191", {"center": v(22.2, 62.17) * mm, "majorRadius": 2.33 * mm, "minorRadius": 1.33 * mm, "majorAxis": v(1, 0)});
            skLineSegment(sketch, "E192", {"start": v(0, 0) * mm, "end": v(53.93, 0) * mm, "construction": true});
            skLineSegment(sketch, "E193", {"start": v(1.32, 58.73) * mm, "end": v(1.32, 62.9) * mm, "construction": true});
            skLineSegment(sketch, "E194", {"start": v(1.32, -62.9) * mm, "end": v(1.32, -58.73) * mm, "construction": true});
            skLineSegment(sketch, "E195", {"start": v(0, -63.1) * mm, "end": v(1.12, -63.1) * mm, "construction": true});
            skLineSegment(sketch, "E196", {"start": v(1.12, 63.1) * mm, "end": v(0, 63.1) * mm, "construction": true});
            skLineSegment(sketch, "E197", {"start": v(1.12, -58.53) * mm, "end": v(0, -58.53) * mm, "construction": true});
            skLineSegment(sketch, "E198", {"start": v(0, 58.53) * mm, "end": v(1.12, 58.53) * mm, "construction": true});
            skLineSegment(sketch, "E199", {"start": v(2.38, -50.63) * mm, "end": v(4.11, -50.63) * mm, "construction": true});
            skLineSegment(sketch, "E200", {"start": v(4.11, 50.63) * mm, "end": v(2.38, 50.63) * mm, "construction": true});
            skLineSegment(sketch, "E201", {"start": v(4.31, -50.83) * mm, "end": v(4.31, -53.94) * mm, "construction": true});
            skLineSegment(sketch, "E202", {"start": v(4.31, 53.94) * mm, "end": v(4.31, 50.83) * mm, "construction": true});
            skLineSegment(sketch, "E203", {"start": v(4.11, -54.14) * mm, "end": v(2.38, -54.14) * mm, "construction": true});
            skLineSegment(sketch, "E204", {"start": v(2.38, 54.14) * mm, "end": v(4.11, 54.14) * mm, "construction": true});
            skEllipse(sketch, "E205", {"center": v(0, 60.82) * mm, "majorRadius": 2.29 * mm, "minorRadius": 1.32 * mm, "majorAxis": v(0, -1)});
            skLineSegment(sketch, "E206", {"start": v(0, -63.1) * mm, "end": v(1.12, -63.1) * mm});
            skLineSegment(sketch, "E207", {"start": v(1.12, 63.1) * mm, "end": v(0, 63.1) * mm});
            skLineSegment(sketch, "E208", {"start": v(0, 63.1) * mm, "end": v(0, 69.85) * mm});
            skLineSegment(sketch, "E209", {"start": v(0, -69.85) * mm, "end": v(0, -63.1) * mm});
            skLineSegment(sketch, "E210", {"start": v(0, 63.1) * mm, "end": v(0, 58.53) * mm, "construction": true});
            skEllipse(sketch, "E211", {"center": v(3.35, 52.39) * mm, "majorRadius": 1.75 * mm, "minorRadius": 0.97 * mm, "majorAxis": v(0, -1)});
            skPoint(sketch, "E212", {"position": v(4.31, 52.39) * mm});
            skLineSegment(sketch, "E213", {"start": v(2.38, 50.63) * mm, "end": v(2.38, 54.14) * mm, "construction": true});
            skSolve(sketch);
        }
        {
            var Q0;
            Q0=makeQuery(id+"F19.imprint","IMPRINT",FACE,{"disambiguationData":[TD([[makeQuery(id+"F19.imprint","IMPRINT",EDGE,{"derivedFrom":sQuery(id+"F19.wireOp",EDGE,"E191")}),1.0]])]});
            var Q1;
            Q1=makeQuery(id+"F19.imprint","IMPRINT",FACE,{"disambiguationData":[TD([[makeQuery(id+"F19.imprint","IMPRINT",EDGE,{"derivedFrom":sQuery(id+"F19.wireOp",EDGE,"E205")}),1.0]])]});
            var Q2;
            Q2=makeQuery(id+"F19.imprint","IMPRINT",FACE,{"disambiguationData":[TD([[makeQuery(id+"F19.imprint","IMPRINT",EDGE,{"derivedFrom":sQuery(id+"F19.wireOp",EDGE,"E211")}),1.0]])]});
            var Q3;
            Q3=sQuery(id+"F19.wireOp",EDGE,"E191");
            var Q4;
            Q4=sQuery(id+"F19.wireOp",EDGE,"E192");
            revolve(context, id + "F20", {"entities" : qUnion([Q0, Q1, Q2]), "surfaceEntities" : qUnion([Q3]), "axis" : qUnion([Q4]), "revolveType" : RevolveType.FULL});
        }
        {
            var Q0;
            Q0=sQuery(id+"F18.wireOp",VERTEX,"E67.end");
            var Q1;
            Q1=qCreatedBy(makeId("Right.planeOp"),FACE);
            cPlane(context, id + "F21", {"entities" : qUnion([Q0, Q1]), "cplaneType" : CPlaneType.PLANE_POINT, "offset" : 25 * mm, "width" : 150 * mm, "height" : 150 * mm});
        }
        {
            var Q0;
            Q0=qCreatedBy(id+"F21.planeOp",FACE);
            var sketch = newSketch(context, id + "F22", { "sketchPlane" : qUnion([Q0])});
            skCircle(sketch, "E214.0", {"center": v(0, 0) * mm, "radius": 56 * mm, "construction": true});
            skArc(sketch, "E215.0", {"start": v(5, 47.74) * mm, "mid": v(0, 48) * mm, "end": v(-5, 47.74) * mm});
            skLineSegment(sketch, "E216", {"start": v(-5, 47.74) * mm, "end": v(-5, 51.5) * mm});
            skLineSegment(sketch, "E217", {"start": v(-1.5, 55) * mm, "end": v(1.5, 55) * mm});
            skLineSegment(sketch, "E218", {"start": v(5, 51.5) * mm, "end": v(5, 47.74) * mm});
            skLineSegment(sketch, "E219", {"start": v(0, 0) * mm, "end": v(0, 70.4) * mm, "construction": true});
            skPoint(sketch, "E220.visualSharp", {"position": v(-5, 55) * mm});
            skArc(sketch, "E220.filletArc", {"start": v(-1.5, 55) * mm, "mid": v(-3.97, 53.97) * mm, "end": v(-5, 51.5) * mm});
            skPoint(sketch, "E221.visualSharp", {"position": v(5, 55) * mm});
            skArc(sketch, "E221.filletArc", {"start": v(5, 51.5) * mm, "mid": v(3.97, 53.97) * mm, "end": v(1.5, 55) * mm});
            skLineSegment(sketch, "E222.1.0", {"start": v(-37.3, 30.22) * mm, "end": v(-39.95, 32.88) * mm});
            skArc(sketch, "E222.1.1", {"start": v(-39.95, 37.83) * mm, "mid": v(-40.98, 35.36) * mm, "end": v(-39.95, 32.88) * mm});
            skLineSegment(sketch, "E222.1.2", {"start": v(-39.95, 37.83) * mm, "end": v(-37.83, 39.95) * mm});
            skArc(sketch, "E222.1.3", {"start": v(-32.88, 39.95) * mm, "mid": v(-35.36, 40.98) * mm, "end": v(-37.83, 39.95) * mm});
            skLineSegment(sketch, "E222.1.4", {"start": v(-32.88, 39.95) * mm, "end": v(-30.22, 37.3) * mm});
            skArc(sketch, "E222.1.5", {"start": v(-30.22, 37.3) * mm, "mid": v(-33.94, 33.94) * mm, "end": v(-37.3, 30.22) * mm});
            skLineSegment(sketch, "E222.2.0", {"start": v(-47.74, -5) * mm, "end": v(-51.5, -5) * mm});
            skArc(sketch, "E222.2.1", {"start": v(-55, -1.5) * mm, "mid": v(-53.97, -3.97) * mm, "end": v(-51.5, -5) * mm});
            skLineSegment(sketch, "E222.2.2", {"start": v(-55, -1.5) * mm, "end": v(-55, 1.5) * mm});
            skArc(sketch, "E222.2.3", {"start": v(-51.5, 5) * mm, "mid": v(-53.97, 3.97) * mm, "end": v(-55, 1.5) * mm});
            skLineSegment(sketch, "E222.2.4", {"start": v(-51.5, 5) * mm, "end": v(-47.74, 5) * mm});
            skArc(sketch, "E222.2.5", {"start": v(-47.74, 5) * mm, "mid": v(-48, 0) * mm, "end": v(-47.74, -5) * mm});
            skLineSegment(sketch, "E222.3.0", {"start": v(-30.22, -37.3) * mm, "end": v(-32.88, -39.95) * mm});
            skArc(sketch, "E222.3.1", {"start": v(-37.83, -39.95) * mm, "mid": v(-35.36, -40.98) * mm, "end": v(-32.88, -39.95) * mm});
            skLineSegment(sketch, "E222.3.2", {"start": v(-37.83, -39.95) * mm, "end": v(-39.95, -37.83) * mm});
            skArc(sketch, "E222.3.3", {"start": v(-39.95, -32.88) * mm, "mid": v(-40.98, -35.36) * mm, "end": v(-39.95, -37.83) * mm});
            skLineSegment(sketch, "E222.3.4", {"start": v(-39.95, -32.88) * mm, "end": v(-37.3, -30.22) * mm});
            skArc(sketch, "E222.3.5", {"start": v(-37.3, -30.22) * mm, "mid": v(-33.94, -33.94) * mm, "end": v(-30.22, -37.3) * mm});
            skLineSegment(sketch, "E222.4.0", {"start": v(5, -47.74) * mm, "end": v(5, -51.5) * mm});
            skArc(sketch, "E222.4.1", {"start": v(1.5, -55) * mm, "mid": v(3.97, -53.97) * mm, "end": v(5, -51.5) * mm});
            skLineSegment(sketch, "E222.4.2", {"start": v(1.5, -55) * mm, "end": v(-1.5, -55) * mm});
            skArc(sketch, "E222.4.3", {"start": v(-5, -51.5) * mm, "mid": v(-3.97, -53.97) * mm, "end": v(-1.5, -55) * mm});
            skLineSegment(sketch, "E222.4.4", {"start": v(-5, -51.5) * mm, "end": v(-5, -47.74) * mm});
            skArc(sketch, "E222.4.5", {"start": v(-5, -47.74) * mm, "mid": v(0, -48) * mm, "end": v(5, -47.74) * mm});
            skLineSegment(sketch, "E222.5.0", {"start": v(37.3, -30.22) * mm, "end": v(39.95, -32.88) * mm});
            skArc(sketch, "E222.5.1", {"start": v(39.95, -37.83) * mm, "mid": v(40.98, -35.36) * mm, "end": v(39.95, -32.88) * mm});
            skLineSegment(sketch, "E222.5.2", {"start": v(39.95, -37.83) * mm, "end": v(37.83, -39.95) * mm});
            skArc(sketch, "E222.5.3", {"start": v(32.88, -39.95) * mm, "mid": v(35.36, -40.98) * mm, "end": v(37.83, -39.95) * mm});
            skLineSegment(sketch, "E222.5.4", {"start": v(32.88, -39.95) * mm, "end": v(30.22, -37.3) * mm});
            skArc(sketch, "E222.5.5", {"start": v(30.22, -37.3) * mm, "mid": v(33.94, -33.94) * mm, "end": v(37.3, -30.22) * mm});
            skLineSegment(sketch, "E222.6.0", {"start": v(47.74, 5) * mm, "end": v(51.5, 5) * mm});
            skArc(sketch, "E222.6.1", {"start": v(55, 1.5) * mm, "mid": v(53.97, 3.97) * mm, "end": v(51.5, 5) * mm});
            skLineSegment(sketch, "E222.6.2", {"start": v(55, 1.5) * mm, "end": v(55, -1.5) * mm});
            skArc(sketch, "E222.6.3", {"start": v(51.5, -5) * mm, "mid": v(53.97, -3.97) * mm, "end": v(55, -1.5) * mm});
            skLineSegment(sketch, "E222.6.4", {"start": v(51.5, -5) * mm, "end": v(47.74, -5) * mm});
            skArc(sketch, "E222.6.5", {"start": v(47.74, -5) * mm, "mid": v(48, 0) * mm, "end": v(47.74, 5) * mm});
            skLineSegment(sketch, "E222.7.0", {"start": v(30.22, 37.3) * mm, "end": v(32.88, 39.95) * mm});
            skArc(sketch, "E222.7.1", {"start": v(37.83, 39.95) * mm, "mid": v(35.36, 40.98) * mm, "end": v(32.88, 39.95) * mm});
            skLineSegment(sketch, "E222.7.2", {"start": v(37.83, 39.95) * mm, "end": v(39.95, 37.83) * mm});
            skArc(sketch, "E222.7.3", {"start": v(39.95, 32.88) * mm, "mid": v(40.98, 35.36) * mm, "end": v(39.95, 37.83) * mm});
            skLineSegment(sketch, "E222.7.4", {"start": v(39.95, 32.88) * mm, "end": v(37.3, 30.22) * mm});
            skArc(sketch, "E222.7.5", {"start": v(37.3, 30.22) * mm, "mid": v(33.94, 33.94) * mm, "end": v(30.22, 37.3) * mm});
            skPoint(sketch, "E223", {"position": v(0, 51.5) * mm});
            skCircle(sketch, "E224.cCircle", {"center": v(0, 51.5) * mm, "radius": 2.5 * mm, "construction": true});
            skLineSegment(sketch, "E224.0", {"start": v(0.75, 54.29) * mm, "end": v(2.8, 52.24) * mm, "construction": true});
            skLineSegment(sketch, "E224.1", {"start": v(2.8, 52.24) * mm, "end": v(2.04, 49.45) * mm, "construction": true});
            skLineSegment(sketch, "E224.2", {"start": v(2.04, 49.45) * mm, "end": v(-0.75, 48.71) * mm, "construction": true});
            skLineSegment(sketch, "E224.3", {"start": v(-0.75, 48.71) * mm, "end": v(-2.8, 50.76) * mm, "construction": true});
            skLineSegment(sketch, "E224.4", {"start": v(-2.8, 50.76) * mm, "end": v(-2.04, 53.55) * mm, "construction": true});
            skLineSegment(sketch, "E224.5", {"start": v(-2.04, 53.55) * mm, "end": v(0.75, 54.29) * mm, "construction": true});
            skPoint(sketch, "E224.0.midPoint", {"position": v(1.77, 53.26) * mm});
            skCircle(sketch, "E225", {"center": v(0, 0) * mm, "radius": 51.5 * mm, "construction": true});
            skLineSegment(sketch, "E226", {"start": v(0, 0) * mm, "end": v(-36.42, 36.42) * mm, "construction": true});
            skLineSegment(sketch, "E227.1.0", {"start": v(0, 0) * mm, "end": v(-51.5, 0) * mm, "construction": true});
            skLineSegment(sketch, "E227.2.0", {"start": v(0, 0) * mm, "end": v(-36.42, -36.42) * mm, "construction": true});
            skLineSegment(sketch, "E227.3.0", {"start": v(0, 0) * mm, "end": v(0, -51.5) * mm, "construction": true});
            skLineSegment(sketch, "E227.4.0", {"start": v(0, 0) * mm, "end": v(36.42, -36.42) * mm, "construction": true});
            skLineSegment(sketch, "E227.5.0", {"start": v(0, 0) * mm, "end": v(51.5, 0) * mm, "construction": true});
            skLineSegment(sketch, "E227.6.0", {"start": v(0, 0) * mm, "end": v(36.42, 36.42) * mm, "construction": true});
            skLineSegment(sketch, "E227.7.0", {"start": v(0, 0) * mm, "end": v(0, 51.5) * mm, "construction": true});
            skSolve(sketch);
        }
        {
            var Q0;
            Q0 = qSketchRegion(id + "F22", true);
            extrude(context, id + "F23", {"entities" : qUnion([Q0]), "operationType" : NewBodyOperationType.REMOVE, "depth" : 25 * mm});
        }
        {
            var Q0;
            Q0=sQuery(id+"F22.wireOp",VERTEX,"E223");
            var Q1;
            Q1=sQuery(id+"F22.wireOp",VERTEX,"E226.end");
            var Q2;
            Q2=sQuery(id+"F22.wireOp",VERTEX,"E227.6.0.end");
            var Q3;
            Q3=sQuery(id+"F22.wireOp",VERTEX,"E227.1.0.end");
            var Q4;
            Q4=sQuery(id+"F22.wireOp",VERTEX,"E227.2.0.end");
            var Q5;
            Q5=sQuery(id+"F22.wireOp",VERTEX,"E227.3.0.end");
            var Q6;
            Q6=sQuery(id+"F22.wireOp",VERTEX,"E227.4.0.end");
            var Q7;
            Q7=sQuery(id+"F22.wireOp",VERTEX,"E227.5.0.end");
            var Q8;
            Q8=makeQuery(id+"F2.opRevolve","SWEPT_BODY",BODY,{"disambiguationData":[OSD([sQuery(id+"F1.wireOp",EDGE,"E0"),sQuery(id+"F1.wireOp",EDGE,"E1"),sQuery(id+"F1.wireOp",EDGE,"E3"),sQuery(id+"F1.wireOp",EDGE,"E4"),sQuery(id+"F1.wireOp",EDGE,"E5"),sQuery(id+"F1.wireOp",EDGE,"E6"),sQuery(id+"F1.wireOp",EDGE,"E8"),sQuery(id+"F1.wireOp",EDGE,"E10"),sQuery(id+"F1.wireOp",EDGE,"E11"),sQuery(id+"F1.wireOp",EDGE,"E12"),sQuery(id+"F1.wireOp",EDGE,"E13"),sQuery(id+"F1.wireOp",EDGE,"E14"),sQuery(id+"F1.wireOp",EDGE,"E16.MirrorCS"),sQuery(id+"F1.wireOp",EDGE,"E17.MirrorCS"),sQuery(id+"F1.wireOp",EDGE,"E18.MirrorCS"),sQuery(id+"F1.wireOp",EDGE,"E19.MirrorCS"),sQuery(id+"F1.wireOp",EDGE,"E20"),sQuery(id+"F1.wireOp",EDGE,"E22"),sQuery(id+"F1.wireOp",EDGE,"E23"),sQuery(id+"F1.wireOp",EDGE,"E24"),sQuery(id+"F1.wireOp",EDGE,"E25"),sQuery(id+"F1.wireOp",EDGE,"E26"),sQuery(id+"F1.wireOp",EDGE,"E27"),sQuery(id+"F1.wireOp",EDGE,"E28"),sQuery(id+"F1.wireOp",EDGE,"E29"),sQuery(id+"F1.wireOp",EDGE,"E30"),sQuery(id+"F1.wireOp",EDGE,"E31")])]});
            hole(context, id + "F24", {"style" : HoleStyle.SIMPLE, "endStyle" : HoleEndStyle.BLIND, "holeDiameter" : 3.15 * mm, "holeDepth" : (getVariable(context, 'M3_Helicoil_Drill_Depth')) * mm, "tappedDepth" : 7.5 * mm, "tapClearance" : 3, "locations" : qUnion([Q0, Q1, Q2, Q3, Q4, Q5, Q6, Q7]), "scope" : qUnion([Q8]), "majorDiameter" : 3 * mm});
        }
        {
            var Q0;
            Q0=makeQuery(id+"F2.opRevolve","SWEPT_FACE",FACE,{"disambiguationData":[OSD([sQuery(id+"F1.wireOp",EDGE,"E1")])]});
            var sketch = newSketch(context, id + "F25", { "sketchPlane" : qUnion([Q0])});
            skCircle(sketch, "E228", {"center": v(0, 0) * mm, "radius": 69.85 * mm});
            skCircle(sketch, "E229", {"center": v(0, 0) * mm, "radius": 63.5 * mm});
            skSolve(sketch);
        }
        {
            var Q0;
            Q0 = qSketchRegion(id + "F25", true);
            extrude(context, id + "F26", {"entities" : qUnion([Q0]), "depth" : 150 * mm});
        }
        {
            var Q0;
            Q0=makeQuery(id+"F2.opRevolve","SWEPT_FACE",FACE,{"disambiguationData":[OSD([sQuery(id+"F1.wireOp",EDGE,"E22")])]});
            var Q1;
            Q1=sQuery(id+"F5.wireOp",VERTEX,"E40");
            cPlane(context, id + "F27", {"entities" : qUnion([Q0, Q1]), "cplaneType" : CPlaneType.PLANE_POINT, "offset" : 25 * mm, "width" : 150 * mm, "height" : 150 * mm});
        }
        {
            var Q0;
            Q0=qCreatedBy(id+"F27.planeOp",FACE);
            var sketch = newSketch(context, id + "F28", { "sketchPlane" : qUnion([Q0])});
            skCircle(sketch, "E230.0", {"center": v(0, 0) * mm, "radius": 63.25 * mm, "construction": true});
            skLineSegment(sketch, "E231", {"start": v(0, 0) * mm, "end": v(0, 63.25) * mm, "construction": true});
            skLineSegment(sketch, "E232", {"start": v(0, 0) * mm, "end": v(24.2, 58.43) * mm, "construction": true});
            skLineSegment(sketch, "E233.1.0", {"start": v(0, 0) * mm, "end": v(-24.2, 58.43) * mm, "construction": true});
            skLineSegment(sketch, "E233.2.0", {"start": v(0, 0) * mm, "end": v(-58.43, 24.2) * mm, "construction": true});
            skLineSegment(sketch, "E233.3.0", {"start": v(0, 0) * mm, "end": v(-58.43, -24.2) * mm, "construction": true});
            skLineSegment(sketch, "E233.4.0", {"start": v(0, 0) * mm, "end": v(-24.2, -58.43) * mm, "construction": true});
            skLineSegment(sketch, "E233.5.0", {"start": v(0, 0) * mm, "end": v(24.2, -58.43) * mm, "construction": true});
            skLineSegment(sketch, "E233.6.0", {"start": v(0, 0) * mm, "end": v(58.43, -24.2) * mm, "construction": true});
            skLineSegment(sketch, "E233.7.0", {"start": v(0, 0) * mm, "end": v(58.43, 24.2) * mm, "construction": true});
            skPoint(sketch, "E234", {"position": v(24.2, 58.43) * mm});
            skPoint(sketch, "E235", {"position": v(58.43, 24.2) * mm});
            skPoint(sketch, "E236", {"position": v(58.43, -24.2) * mm});
            skPoint(sketch, "E237", {"position": v(24.2, -58.43) * mm});
            skPoint(sketch, "E238", {"position": v(-24.2, -58.43) * mm});
            skPoint(sketch, "E239", {"position": v(-58.43, -24.2) * mm});
            skPoint(sketch, "E240", {"position": v(-58.43, 24.2) * mm});
            skPoint(sketch, "E241", {"position": v(-24.2, 58.43) * mm});
            skSolve(sketch);
        }
        {
            var Q0;
            Q0=sQuery(id+"F28.wireOp",VERTEX,"E234");
            var Q1;
            Q1=sQuery(id+"F28.wireOp",EDGE,"E232");
            cPlane(context, id + "F29", {"entities" : qUnion([Q0, Q1]), "cplaneType" : CPlaneType.LINE_POINT, "offset" : 25 * mm, "width" : 150 * mm, "height" : 150 * mm});
        }
        {
            var Q0;
            Q0=sQuery(id+"F28.wireOp",EDGE,"E233.7.0");
            var Q1;
            Q1=sQuery(id+"F28.wireOp",VERTEX,"E235");
            cPlane(context, id + "F30", {"entities" : qUnion([Q0, Q1]), "cplaneType" : CPlaneType.LINE_POINT, "offset" : 25 * mm, "width" : 150 * mm, "height" : 150 * mm});
        }
        {
            var Q0;
            Q0=sQuery(id+"F28.wireOp",EDGE,"E233.6.0");
            var Q1;
            Q1=sQuery(id+"F28.wireOp",VERTEX,"E236");
            cPlane(context, id + "F31", {"entities" : qUnion([Q0, Q1]), "cplaneType" : CPlaneType.LINE_POINT, "offset" : 25 * mm, "width" : 150 * mm, "height" : 150 * mm});
        }
        {
            var Q0;
            Q0=sQuery(id+"F28.wireOp",EDGE,"E233.5.0");
            var Q1;
            Q1=sQuery(id+"F28.wireOp",VERTEX,"E237");
            cPlane(context, id + "F32", {"entities" : qUnion([Q0, Q1]), "cplaneType" : CPlaneType.LINE_POINT, "offset" : 25 * mm, "width" : 150 * mm, "height" : 150 * mm});
        }
        {
            var Q0;
            Q0=sQuery(id+"F28.wireOp",EDGE,"E233.4.0");
            var Q1;
            Q1=sQuery(id+"F28.wireOp",VERTEX,"E238");
            cPlane(context, id + "F33", {"entities" : qUnion([Q0, Q1]), "cplaneType" : CPlaneType.LINE_POINT, "offset" : 25 * mm, "width" : 150 * mm, "height" : 150 * mm});
        }
        {
            var Q0;
            Q0=sQuery(id+"F28.wireOp",VERTEX,"E239");
            var Q1;
            Q1=sQuery(id+"F28.wireOp",EDGE,"E233.3.0");
            cPlane(context, id + "F34", {"entities" : qUnion([Q0, Q1]), "cplaneType" : CPlaneType.LINE_POINT, "offset" : 25 * mm, "width" : 150 * mm, "height" : 150 * mm});
        }
        {
            var Q0;
            Q0=sQuery(id+"F28.wireOp",VERTEX,"E240");
            var Q1;
            Q1=sQuery(id+"F28.wireOp",EDGE,"E233.2.0");
            cPlane(context, id + "F35", {"entities" : qUnion([Q0, Q1]), "cplaneType" : CPlaneType.LINE_POINT, "offset" : 25 * mm, "width" : 150 * mm, "height" : 150 * mm});
        }
        {
            var Q0;
            Q0=sQuery(id+"F28.wireOp",EDGE,"E233.1.0");
            var Q1;
            Q1=sQuery(id+"F28.wireOp",VERTEX,"E241");
            cPlane(context, id + "F36", {"entities" : qUnion([Q0, Q1]), "cplaneType" : CPlaneType.LINE_POINT, "offset" : 25 * mm, "width" : 150 * mm, "height" : 150 * mm});
        }
        {
            var Q0;
            Q0=qCreatedBy(id+"F29.planeOp",FACE);
            var sketch = newSketch(context, id + "F37", { "sketchPlane" : qUnion([Q0])});
            skPoint(sketch, "E242.0", {"position": v(15.25, 0) * mm});
            skSolve(sketch);
        }
        {
            var Q0;
            Q0=qCreatedBy(id+"F30.planeOp",FACE);
            var sketch = newSketch(context, id + "F38", { "sketchPlane" : qUnion([Q0])});
            skPoint(sketch, "E243.0", {"position": v(15.25, 0) * mm});
            skSolve(sketch);
        }
        {
            var Q0;
            Q0=qCreatedBy(id+"F31.planeOp",FACE);
            var sketch = newSketch(context, id + "F39", { "sketchPlane" : qUnion([Q0])});
            skPoint(sketch, "E244.0", {"position": v(15.25, 0) * mm});
            skSolve(sketch);
        }
        {
            var Q0;
            Q0=qCreatedBy(id+"F32.planeOp",FACE);
            var sketch = newSketch(context, id + "F40", { "sketchPlane" : qUnion([Q0])});
            skPoint(sketch, "E245.0", {"position": v(15.25, 0) * mm});
            skSolve(sketch);
        }
        {
            var Q0;
            Q0=qCreatedBy(id+"F33.planeOp",FACE);
            var sketch = newSketch(context, id + "F41", { "sketchPlane" : qUnion([Q0])});
            skPoint(sketch, "E246.0", {"position": v(15.25, 0) * mm});
            skSolve(sketch);
        }
        {
            var Q0;
            Q0=qCreatedBy(id+"F34.planeOp",FACE);
            var sketch = newSketch(context, id + "F42", { "sketchPlane" : qUnion([Q0])});
            skPoint(sketch, "E247.0", {"position": v(-15.25, 0) * mm});
            skSolve(sketch);
        }
        {
            var Q0;
            Q0=qCreatedBy(id+"F35.planeOp",FACE);
            var sketch = newSketch(context, id + "F43", { "sketchPlane" : qUnion([Q0])});
            skPoint(sketch, "E248.0", {"position": v(-15.25, 0) * mm});
            skSolve(sketch);
        }
        {
            var Q0;
            Q0=qCreatedBy(id+"F36.planeOp",FACE);
            var sketch = newSketch(context, id + "F44", { "sketchPlane" : qUnion([Q0])});
            skPoint(sketch, "E249.0", {"position": v(15.25, 0) * mm});
            skSolve(sketch);
        }
        {
            var Q0;
            Q0=sQuery(id+"F37.wireOp",VERTEX,"E242.0");
            var Q1;
            Q1=sQuery(id+"F43.wireOp",VERTEX,"E248.0");
            var Q2;
            Q2=sQuery(id+"F42.wireOp",VERTEX,"E247.0");
            var Q3;
            Q3=sQuery(id+"F41.wireOp",VERTEX,"E246.0");
            var Q4;
            Q4=sQuery(id+"F40.wireOp",VERTEX,"E245.0");
            var Q5;
            Q5=sQuery(id+"F39.wireOp",VERTEX,"E244.0");
            var Q6;
            Q6=sQuery(id+"F38.wireOp",VERTEX,"E243.0");
            var Q7;
            Q7=sQuery(id+"F44.wireOp",VERTEX,"E249.0");
            var Q8;
            Q8=makeQuery(id+"F2.opRevolve","SWEPT_BODY",BODY,{"disambiguationData":[OSD([sQuery(id+"F1.wireOp",EDGE,"E0"),sQuery(id+"F1.wireOp",EDGE,"E1"),sQuery(id+"F1.wireOp",EDGE,"E3"),sQuery(id+"F1.wireOp",EDGE,"E4"),sQuery(id+"F1.wireOp",EDGE,"E5"),sQuery(id+"F1.wireOp",EDGE,"E6"),sQuery(id+"F1.wireOp",EDGE,"E8"),sQuery(id+"F1.wireOp",EDGE,"E10"),sQuery(id+"F1.wireOp",EDGE,"E11"),sQuery(id+"F1.wireOp",EDGE,"E12"),sQuery(id+"F1.wireOp",EDGE,"E13"),sQuery(id+"F1.wireOp",EDGE,"E14"),sQuery(id+"F1.wireOp",EDGE,"E16.MirrorCS"),sQuery(id+"F1.wireOp",EDGE,"E17.MirrorCS"),sQuery(id+"F1.wireOp",EDGE,"E18.MirrorCS"),sQuery(id+"F1.wireOp",EDGE,"E19.MirrorCS"),sQuery(id+"F1.wireOp",EDGE,"E20"),sQuery(id+"F1.wireOp",EDGE,"E22"),sQuery(id+"F1.wireOp",EDGE,"E23"),sQuery(id+"F1.wireOp",EDGE,"E24"),sQuery(id+"F1.wireOp",EDGE,"E25"),sQuery(id+"F1.wireOp",EDGE,"E26"),sQuery(id+"F1.wireOp",EDGE,"E27"),sQuery(id+"F1.wireOp",EDGE,"E28"),sQuery(id+"F1.wireOp",EDGE,"E29"),sQuery(id+"F1.wireOp",EDGE,"E30"),sQuery(id+"F1.wireOp",EDGE,"E31")])]});
            hole(context, id + "F45", {"style" : HoleStyle.SIMPLE, "endStyle" : HoleEndStyle.BLIND, "standardTappedOrClearance" : lookupTablePath({ "standard" : "ISO", "engagement" : "75%", "pitch" : "0.5 mm", "size" : "M3", "type" : "Tapped" }), "standardBlindInLast" : lookupTablePath({ "standard" : "ISO", "engagement" : "75%", "pitch" : "0.5 mm", "size" : "M3", "type" : "Tapped" }), "holeDiameter" : 2.5 * mm, "showTappedDepth" : true, "holeDepth" : (getVariable(context, 'M3_Helicoil_Drill_Depth')) * mm, "tappedDepth" : 7.5 * mm, "tapClearance" : 3, "locations" : qUnion([Q0, Q1, Q2, Q3, Q4, Q5, Q6, Q7]), "scope" : qUnion([Q8]), "majorDiameter" : 3 * mm});
        }
        {
            var Q0;
            Q0=makeQuery(id+"F23.boolean.opBoolean","COPY",FACE,{"derivedFrom":makeQuery(id+"F23.opExtrude","CAP_FACE",FACE,{"disambiguationData":[OSD([sQuery(id+"F22.wireOp",EDGE,"E215.0"),sQuery(id+"F22.wireOp",EDGE,"E216"),sQuery(id+"F22.wireOp",EDGE,"E217"),sQuery(id+"F22.wireOp",EDGE,"E218"),sQuery(id+"F22.wireOp",EDGE,"E220.filletArc"),sQuery(id+"F22.wireOp",EDGE,"E221.filletArc")])],"isStart":true})});
            var sketch = newSketch(context, id + "F46", { "sketchPlane" : qUnion([Q0])});
            skCircle(sketch, "E250.cCircle", {"center": v(0, 51.5) * mm, "radius": 2.5 * mm, "construction": true});
            skLineSegment(sketch, "E250.0", {"start": v(2.87, 51.8) * mm, "end": v(1.7, 49.17) * mm});
            skLineSegment(sketch, "E250.1", {"start": v(1.7, 49.17) * mm, "end": v(-1.17, 48.86) * mm});
            skLineSegment(sketch, "E250.2", {"start": v(-1.17, 48.86) * mm, "end": v(-2.87, 51.2) * mm});
            skLineSegment(sketch, "E250.3", {"start": v(-2.87, 51.2) * mm, "end": v(-1.7, 53.83) * mm});
            skLineSegment(sketch, "E250.4", {"start": v(-1.7, 53.83) * mm, "end": v(1.17, 54.14) * mm});
            skLineSegment(sketch, "E250.5", {"start": v(1.17, 54.14) * mm, "end": v(2.87, 51.8) * mm});
            skPoint(sketch, "E250.0.midPoint", {"position": v(2.28, 50.48) * mm});
            skSolve(sketch);
        }
        {
            var Q0;
            Q0 = qSketchRegion(id + "F46", true);
            extrude(context, id + "F47", {"entities" : qUnion([Q0]), "depth" : 20 * mm});
        }
    });
